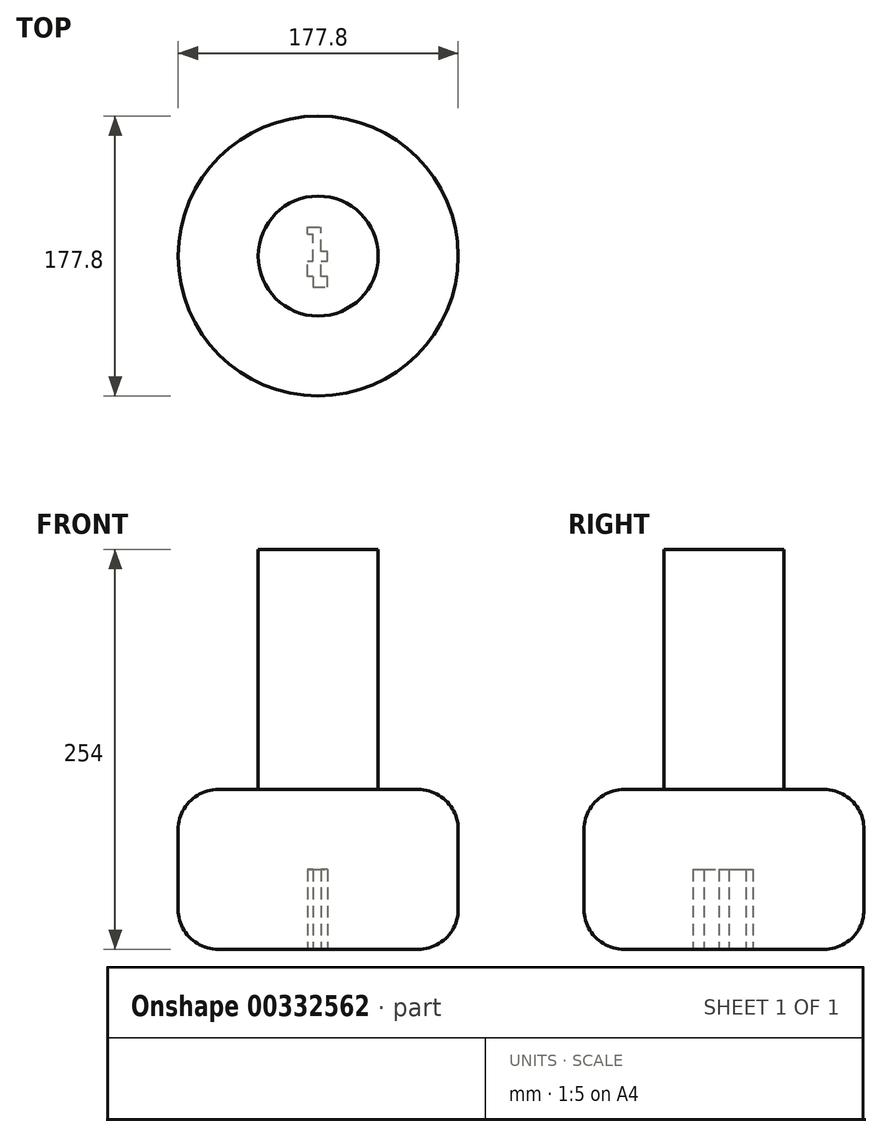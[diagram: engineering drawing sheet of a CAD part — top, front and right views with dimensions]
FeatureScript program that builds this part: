
annotation { "Feature Type Name" : "Feature", "Feature Type Description" : "" }
export const myFeature = defineFeature(function(context is Context, id is Id, definition is map)
    precondition{}
    {
        {
            var Q0;
            Q0=qCreatedBy(makeId("Top.planeOp"),FACE);
            var sketch = newSketch(context, id + "F0", { "sketchPlane" : qUnion([Q0])});
            skCircle(sketch, "E0", {"center": v(0, 0) * mm, "radius": 88.9 * mm});
            skCircle(sketch, "E1.0", {"center": v(0, 0) * mm, "radius": 38.1 * mm});
            skSolve(sketch);
        }
        {
            var Q0;
            Q0=makeQuery(id+"F0.imprint","IMPRINT",FACE,{"disambiguationData":[TD([[makeQuery(id+"F0.imprint","IMPRINT",EDGE,{"derivedFrom":sQuery(id+"F0.wireOp",EDGE,"E0")}),1.0]])]});
            extrude(context, id + "F1", {"entities" : qUnion([Q0]), "depth" : 101.6 * mm});
        }
        {
            var Q0;
            Q0=makeQuery(id+"F0.imprint","IMPRINT",FACE,{"disambiguationData":[TD([[makeQuery(id+"F0.imprint","IMPRINT",EDGE,{"derivedFrom":sQuery(id+"F0.wireOp",EDGE,"E1.0")}),1.0]])]});
            extrude(context, id + "F2", {"entities" : qUnion([Q0]), "operationType" : NewBodyOperationType.ADD, "depth" : 254 * mm});
        }
        {
            var Q0;
            Q0=makeQuery(id+"F1.opExtrude","CAP_EDGE",EDGE,{"disambiguationData":[OSD([sQuery(id+"F0.wireOp",EDGE,"E0")])],"isStart":false});
            fillet(context, id + "F3", {"entities" : qUnion([Q0]), "radius" : 25.4 * mm, "tangentPropagation" : true, "allowEdgeOverflow" : false});
        }
        {
            var Q0;
            Q0=makeQuery(id+"F1.opExtrude","CAP_EDGE",EDGE,{"disambiguationData":[OSD([sQuery(id+"F0.wireOp",EDGE,"E0")])],"isStart":true});
            fillet(context, id + "F4", {"entities" : qUnion([Q0]), "radius" : 25.4 * mm, "tangentPropagation" : true, "allowEdgeOverflow" : false});
        }
        {
            var Q0;
            {var subQ0=sQuery(id+"F0.wireOp",EDGE,"E1.0");Q0=makeQuery(id+"F2.boolean.opBoolean","MERGE",FACE,{"derivedFrom":[makeQuery(id+"F1.opExtrude","CAP_FACE",FACE,{"disambiguationData":[OSD([sQuery(id+"F0.wireOp",EDGE,"E0"),subQ0])],"isStart":true}),makeQuery(id+"F2.opExtrude","CAP_FACE",FACE,{"disambiguationData":[OSD([subQ0])],"isStart":true})]});}
            var sketch = newSketch(context, id + "F5", { "sketchPlane" : qUnion([Q0])});
            skLineSegment(sketch, "E2.bottom", {"start": v(-3.14, 19.71) * mm, "end": v(6.03, 19.71) * mm});
            skLineSegment(sketch, "E2.top", {"start": v(-6.67, -18.39) * mm, "end": v(1.82, -18.39) * mm});
            skLineSegment(sketch, "E2.left", {"start": v(-6.67, 12.9) * mm, "end": v(-6.67, 3.3) * mm});
            skLineSegment(sketch, "E2.right", {"start": v(6.03, 19.71) * mm, "end": v(6.03, 12.9) * mm});
            skLineSegment(sketch, "E3", {"start": v(6.03, 12.9) * mm, "end": v(1.82, 12.9) * mm});
            skLineSegment(sketch, "E4", {"start": v(1.82, 12.9) * mm, "end": v(1.82, 3.3) * mm});
            skLineSegment(sketch, "E5", {"start": v(1.82, 3.3) * mm, "end": v(6.03, 3.3) * mm});
            skLineSegment(sketch, "E6", {"start": v(-6.67, 3.3) * mm, "end": v(-3.14, 3.3) * mm});
            skLineSegment(sketch, "E7", {"start": v(-3.14, 3.3) * mm, "end": v(-3.14, -13.9) * mm});
            skLineSegment(sketch, "E8", {"start": v(-6.67, -13.9) * mm, "end": v(-3.14, -13.9) * mm});
            skLineSegment(sketch, "E9", {"start": v(6.03, -2.98) * mm, "end": v(1.82, -2.98) * mm});
            skLineSegment(sketch, "E10", {"start": v(1.82, -2.98) * mm, "end": v(1.82, -18.39) * mm});
            skLineSegment(sketch, "E11.trimOffspring", {"start": v(6.03, 3.3) * mm, "end": v(6.03, -2.98) * mm});
            skLineSegment(sketch, "E12.trimOffspring", {"start": v(-6.67, -13.9) * mm, "end": v(-6.67, -18.39) * mm});
            skLineSegment(sketch, "E13", {"start": v(-3.14, 12.9) * mm, "end": v(-6.67, 12.9) * mm});
            skLineSegment(sketch, "E14", {"start": v(-6.67, 12.9) * mm, "end": v(-3.14, 12.9) * mm});
            skLineSegment(sketch, "E15", {"start": v(-3.14, 12.9) * mm, "end": v(-3.14, 19.71) * mm});
            skSolve(sketch);
        }
        {
            var Q0;
            Q0=makeQuery(id+"F5.imprint","IMPRINT",FACE,{"disambiguationData":[TD([[makeQuery(id+"F5.imprint","IMPRINT",EDGE,{"derivedFrom":sQuery(id+"F5.wireOp",EDGE,"E2.bottom")}),-1.0]])]});
            extrude(context, id + "F6", {"entities" : qUnion([Q0]), "operationType" : NewBodyOperationType.REMOVE, "oppositeDirection" : true, "depth" : 50.8 * mm});
        }
    });
